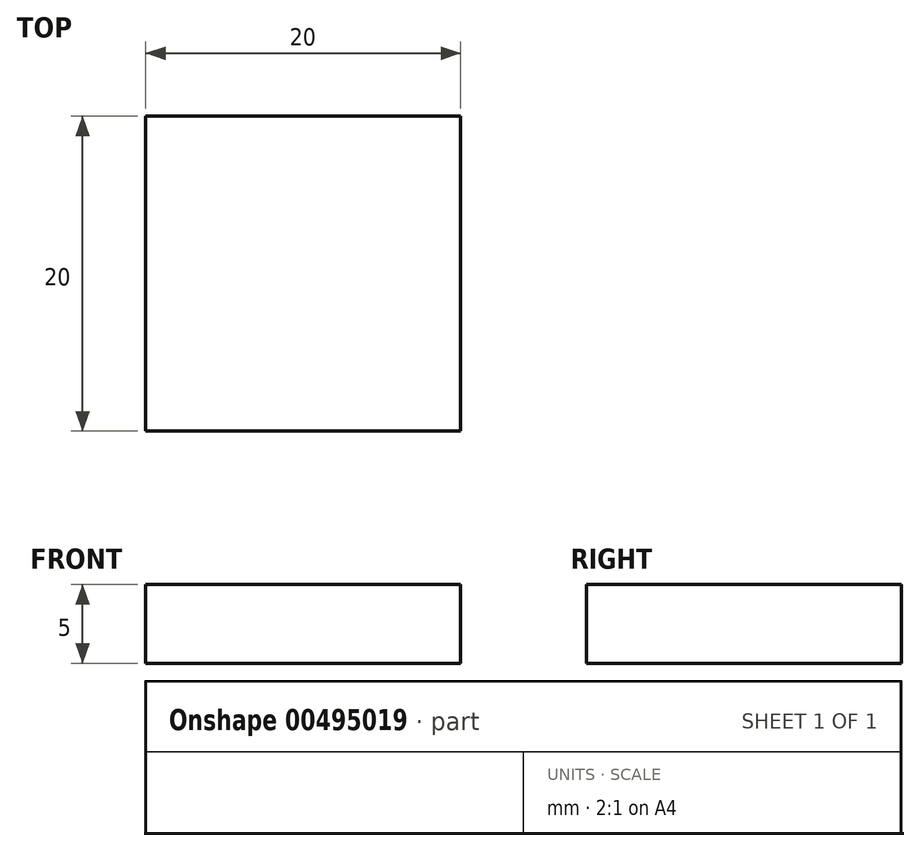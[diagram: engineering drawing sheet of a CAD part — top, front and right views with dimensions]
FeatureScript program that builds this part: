
annotation { "Feature Type Name" : "Feature", "Feature Type Description" : "" }
export const myFeature = defineFeature(function(context is Context, id is Id, definition is map)
    precondition{}
    {
        {
            var Q0;
            Q0=qCreatedBy(makeId("Top.planeOp"),FACE);
            var sketch = newSketch(context, id + "F0", { "sketchPlane" : qUnion([Q0])});
            skLineSegment(sketch, "E0.bottom", {"start": v(10, 10) * mm, "end": v(-10, 10) * mm});
            skLineSegment(sketch, "E0.top", {"start": v(10, -10) * mm, "end": v(-10, -10) * mm});
            skLineSegment(sketch, "E0.left", {"start": v(10, 10) * mm, "end": v(10, -10) * mm});
            skLineSegment(sketch, "E0.right", {"start": v(-10, 10) * mm, "end": v(-10, -10) * mm});
            skPoint(sketch, "E0.middle", {"position": v(0, 0) * mm});
            skSolve(sketch);
        }
        {
            var Q0;
            Q0=makeQuery(id+"F0.imprint","IMPRINT",FACE,{"disambiguationData":[TD([[makeQuery(id+"F0.imprint","IMPRINT",EDGE,{"derivedFrom":sQuery(id+"F0.wireOp",EDGE,"E0.bottom")}),1.0]])]});
            extrude(context, id + "F1", {"entities" : qUnion([Q0]), "depth" : 5 * mm, "offsetDistance" : 25.4 * mm});
        }
    });
